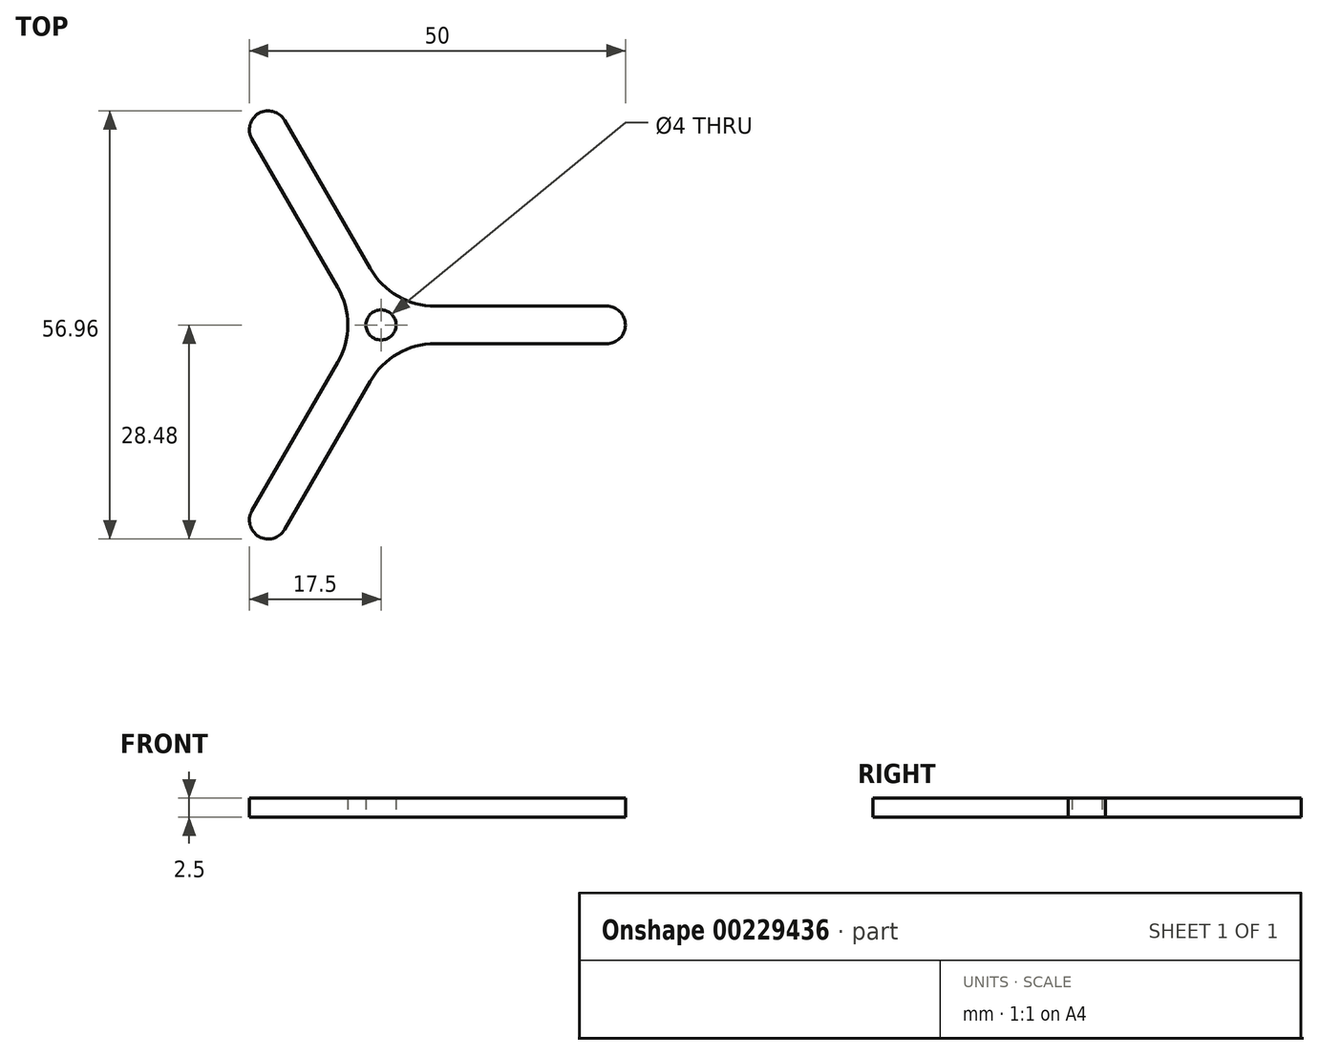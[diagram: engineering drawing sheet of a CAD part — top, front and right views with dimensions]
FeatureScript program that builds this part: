
annotation { "Feature Type Name" : "Feature", "Feature Type Description" : "" }
export const myFeature = defineFeature(function(context is Context, id is Id, definition is map)
    precondition{}
    {
        {
            var Q0;
            Q0=qCreatedBy(makeId("Top.planeOp"),FACE);
            var sketch = newSketch(context, id + "F0", { "sketchPlane" : qUnion([Q0])});
            skCircle(sketch, "E0", {"center": v(30, 0) * mm, "radius": 2.5 * mm});
            skCircle(sketch, "E1", {"center": v(0, 0) * mm, "radius": 2.5 * mm});
            skLineSegment(sketch, "E2", {"start": v(30, 0) * mm, "end": v(0, 0) * mm});
            skLineSegment(sketch, "E3", {"start": v(0, -2.5) * mm, "end": v(30, -2.5) * mm});
            skLineSegment(sketch, "E4.MirrorCS", {"start": v(0, 2.5) * mm, "end": v(30, 2.5) * mm});
            skLineSegment(sketch, "E5.1.1", {"start": v(2.17, 1.25) * mm, "end": v(-12.83, 27.23) * mm});
            skLineSegment(sketch, "E5.1.2", {"start": v(-2.17, -1.25) * mm, "end": v(-17.17, 24.73) * mm});
            skCircle(sketch, "E5.1.3", {"center": v(-15, 25.98) * mm, "radius": 2.5 * mm});
            skLineSegment(sketch, "E5.1.4", {"start": v(-15, 25.98) * mm, "end": v(0, 0) * mm});
            skLineSegment(sketch, "E5.2.1", {"start": v(-2.17, 1.25) * mm, "end": v(-17.17, -24.73) * mm});
            skLineSegment(sketch, "E5.2.2", {"start": v(2.17, -1.25) * mm, "end": v(-12.83, -27.23) * mm});
            skCircle(sketch, "E5.2.3", {"center": v(-15, -25.98) * mm, "radius": 2.5 * mm});
            skLineSegment(sketch, "E5.2.4", {"start": v(-15, -25.98) * mm, "end": v(0, 0) * mm});
            skSolve(sketch);
        }
        {
            var Q0;
            {var subQ0=sQuery(id+"F0.wireOp",EDGE,"E1");var subQ1=makeQuery(id+"F0.imprint","INTERSECT",VERTEX,{"derivedFrom":[sQuery(id+"F0.wireOp",EDGE,"E3"),subQ0]});Q0=makeQuery(id+"F0.imprint","IMPRINT",FACE,{"disambiguationData":[TD([[makeQuery(id+"F0.imprint","IMPRINT",EDGE,{"disambiguationData":[TD([[subQ1,1.0]])],"derivedFrom":subQ0}),1.0]])]});}
            var Q1;
            {var subQ0=sQuery(id+"F0.wireOp",EDGE,"E1");var subQ4=makeQuery(id+"F0.imprint","INTERSECT",VERTEX,{"derivedFrom":[subQ0,sQuery(id+"F0.wireOp",EDGE,"E5.2.1")]});Q1=makeQuery(id+"F0.imprint","IMPRINT",FACE,{"disambiguationData":[TD([[makeQuery(id+"F0.imprint","IMPRINT",EDGE,{"disambiguationData":[TD([[subQ4,1.0]])],"derivedFrom":subQ0}),1.0]])]});}
            var Q2;
            {var subQ0=sQuery(id+"F0.wireOp",EDGE,"E0");var subQ1=makeQuery(id+"F0.imprint","INTERSECT",VERTEX,{"derivedFrom":[subQ0,sQuery(id+"F0.wireOp",EDGE,"E4.MirrorCS")]});Q2=makeQuery(id+"F0.imprint","IMPRINT",FACE,{"disambiguationData":[TD([[makeQuery(id+"F0.imprint","IMPRINT",EDGE,{"disambiguationData":[TD([[subQ1,-1.0]])],"derivedFrom":subQ0}),1.0]])]});}
            var Q3;
            {var subQ0=sQuery(id+"F0.wireOp",EDGE,"E5.1.3");var subQ1=makeQuery(id+"F0.imprint","INTERSECT",VERTEX,{"derivedFrom":[sQuery(id+"F0.wireOp",EDGE,"E5.1.2"),subQ0]});Q3=makeQuery(id+"F0.imprint","IMPRINT",FACE,{"disambiguationData":[TD([[makeQuery(id+"F0.imprint","IMPRINT",EDGE,{"disambiguationData":[TD([[subQ1,-1.0]])],"derivedFrom":subQ0}),1.0]])]});}
            var Q4;
            {var subQ0=sQuery(id+"F0.wireOp",EDGE,"E5.2.3");var subQ1=makeQuery(id+"F0.imprint","INTERSECT",VERTEX,{"derivedFrom":[sQuery(id+"F0.wireOp",EDGE,"E5.2.2"),subQ0]});Q4=makeQuery(id+"F0.imprint","IMPRINT",FACE,{"disambiguationData":[TD([[makeQuery(id+"F0.imprint","IMPRINT",EDGE,{"disambiguationData":[TD([[subQ1,-1.0]])],"derivedFrom":subQ0}),1.0]])]});}
            var Q5;
            {var subQ3=sQuery(id+"F0.wireOp",EDGE,"E4.MirrorCS");var subQ5=sQuery(id+"F0.wireOp",EDGE,"E0");var subQ6=makeQuery(id+"F0.imprint","INTERSECT",VERTEX,{"derivedFrom":[subQ5,subQ3]});Q5=makeQuery(id+"F0.imprint","IMPRINT",FACE,{"disambiguationData":[TD([[makeQuery(id+"F0.imprint","IMPRINT",EDGE,{"disambiguationData":[TD([[subQ6,-1.0]])],"derivedFrom":subQ5}),-1.0]])]});}
            var Q6;
            {var subQ5=sQuery(id+"F0.wireOp",EDGE,"E3");var subQ6=sQuery(id+"F0.wireOp",EDGE,"E0");var subQ7=makeQuery(id+"F0.imprint","INTERSECT",VERTEX,{"derivedFrom":[subQ6,subQ5]});Q6=makeQuery(id+"F0.imprint","IMPRINT",FACE,{"disambiguationData":[TD([[makeQuery(id+"F0.imprint","IMPRINT",EDGE,{"disambiguationData":[TD([[subQ7,1.0]])],"derivedFrom":subQ6}),-1.0]])]});}
            var Q7;
            {var subQ5=sQuery(id+"F0.wireOp",EDGE,"E3");var subQ7=sQuery(id+"F0.wireOp",EDGE,"E1");var subQ8=makeQuery(id+"F0.imprint","INTERSECT",VERTEX,{"derivedFrom":[subQ5,subQ7]});Q7=makeQuery(id+"F0.imprint","IMPRINT",FACE,{"disambiguationData":[TD([[makeQuery(id+"F0.imprint","IMPRINT",EDGE,{"disambiguationData":[TD([[subQ8,-1.0]])],"derivedFrom":subQ5}),-1.0]])]});}
            var Q8;
            {var subQ3=sQuery(id+"F0.wireOp",EDGE,"E1");var subQ7=sQuery(id+"F0.wireOp",EDGE,"E4.MirrorCS");var subQ8=makeQuery(id+"F0.imprint","INTERSECT",VERTEX,{"derivedFrom":[subQ7,subQ3]});Q8=makeQuery(id+"F0.imprint","IMPRINT",FACE,{"disambiguationData":[TD([[makeQuery(id+"F0.imprint","IMPRINT",EDGE,{"disambiguationData":[TD([[subQ8,-1.0]])],"derivedFrom":subQ7}),1.0]])]});}
            var Q9;
            {var subQ5=sQuery(id+"F0.wireOp",EDGE,"E5.1.2");var subQ7=sQuery(id+"F0.wireOp",EDGE,"E1");var subQ8=makeQuery(id+"F0.imprint","INTERSECT",VERTEX,{"derivedFrom":[subQ5,subQ7]});Q9=makeQuery(id+"F0.imprint","IMPRINT",FACE,{"disambiguationData":[TD([[makeQuery(id+"F0.imprint","IMPRINT",EDGE,{"disambiguationData":[TD([[subQ8,-1.0]])],"derivedFrom":subQ5}),1.0]])]});}
            var Q10;
            {var subQ5=sQuery(id+"F0.wireOp",EDGE,"E5.1.3");var subQ6=sQuery(id+"F0.wireOp",EDGE,"E5.1.2");var subQ7=makeQuery(id+"F0.imprint","INTERSECT",VERTEX,{"derivedFrom":[subQ6,subQ5]});Q10=makeQuery(id+"F0.imprint","IMPRINT",FACE,{"disambiguationData":[TD([[makeQuery(id+"F0.imprint","IMPRINT",EDGE,{"disambiguationData":[TD([[subQ7,1.0]])],"derivedFrom":subQ6}),-1.0]])]});}
            var Q11;
            {var subQ3=sQuery(id+"F0.wireOp",EDGE,"E1");var subQ6=makeQuery(id+"F0.imprint","INTERSECT",VERTEX,{"derivedFrom":[sQuery(id+"F0.wireOp",EDGE,"E5.1.1"),subQ3]});Q11=makeQuery(id+"F0.imprint","IMPRINT",FACE,{"disambiguationData":[TD([[makeQuery(id+"F0.imprint","IMPRINT",EDGE,{"disambiguationData":[TD([[subQ6,1.0]])],"derivedFrom":subQ3}),1.0]])]});}
            var Q12;
            {var subQ0=sQuery(id+"F0.wireOp",EDGE,"E1");var subQ1=sQuery(id+"F0.wireOp",EDGE,"E3");var subQ2=makeQuery(id+"F0.imprint","INTERSECT",VERTEX,{"derivedFrom":[subQ1,subQ0]});Q12=makeQuery(id+"F0.imprint","IMPRINT",FACE,{"disambiguationData":[TD([[makeQuery(id+"F0.imprint","IMPRINT",EDGE,{"disambiguationData":[TD([[subQ2,-1.0]])],"derivedFrom":subQ1}),1.0]])]});}
            var Q13;
            {var subQ0=sQuery(id+"F0.wireOp",EDGE,"E1");var subQ1=sQuery(id+"F0.wireOp",EDGE,"E4.MirrorCS");var subQ2=makeQuery(id+"F0.imprint","INTERSECT",VERTEX,{"derivedFrom":[subQ1,subQ0]});Q13=makeQuery(id+"F0.imprint","IMPRINT",FACE,{"disambiguationData":[TD([[makeQuery(id+"F0.imprint","IMPRINT",EDGE,{"disambiguationData":[TD([[subQ2,-1.0]])],"derivedFrom":subQ1}),-1.0]])]});}
            var Q14;
            {var subQ0=sQuery(id+"F0.wireOp",EDGE,"E1");var subQ1=sQuery(id+"F0.wireOp",EDGE,"E5.1.2");var subQ2=makeQuery(id+"F0.imprint","INTERSECT",VERTEX,{"derivedFrom":[subQ1,subQ0]});Q14=makeQuery(id+"F0.imprint","IMPRINT",FACE,{"disambiguationData":[TD([[makeQuery(id+"F0.imprint","IMPRINT",EDGE,{"disambiguationData":[TD([[subQ2,-1.0]])],"derivedFrom":subQ1}),-1.0]])]});}
            extrude(context, id + "F1", {"entities" : qUnion([Q0, Q1, Q2, Q3, Q4, Q5, Q6, Q7, Q8, Q9, Q10, Q11, Q12, Q13, Q14]), "depth" : 2.5 * mm});
        }
        {
            var Q0;
            Q0=qCreatedBy(makeId("Top.planeOp"),FACE);
            var sketch = newSketch(context, id + "F2", { "sketchPlane" : qUnion([Q0])});
            skPoint(sketch, "E6", {"position": v(0, 0) * mm});
            skSolve(sketch);
        }
        {
            var Q0;
            Q0=sQuery(id+"F2.wireOp",VERTEX,"E6");
            var Q1;
            Q1=makeQuery(id+"F1.opExtrude","SWEPT_BODY",BODY,{"disambiguationData":[OSD([sQuery(id+"F0.wireOp",EDGE,"E0"),sQuery(id+"F0.wireOp",EDGE,"E3"),sQuery(id+"F0.wireOp",EDGE,"E4.MirrorCS"),sQuery(id+"F0.wireOp",EDGE,"E5.1.1"),sQuery(id+"F0.wireOp",EDGE,"E5.1.2"),sQuery(id+"F0.wireOp",EDGE,"E5.1.3"),sQuery(id+"F0.wireOp",EDGE,"E5.2.1"),sQuery(id+"F0.wireOp",EDGE,"E5.2.2"),sQuery(id+"F0.wireOp",EDGE,"E5.2.3")])]});
            hole(context, id + "F3", {"style" : HoleStyle.SIMPLE, "endStyle" : HoleEndStyle.THROUGH, "oppositeDirection" : true, "holeDiameter" : 4 * mm, "locations" : qUnion([Q0]), "scope" : qUnion([Q1]), "isTappedThrough" : true});
        }
        {
            var Q0;
            Q0=makeQuery(id+"F1.opExtrude","SWEPT_EDGE",EDGE,{"disambiguationData":[OSD([sQuery(id+"F0.wireOp",EDGE,"E3"),sQuery(id+"F0.wireOp",EDGE,"E5.2.2")])]});
            var Q1;
            Q1=makeQuery(id+"F1.opExtrude","SWEPT_EDGE",EDGE,{"disambiguationData":[OSD([sQuery(id+"F0.wireOp",EDGE,"E5.1.2"),sQuery(id+"F0.wireOp",EDGE,"E5.2.1")])]});
            var Q2;
            Q2=makeQuery(id+"F1.opExtrude","SWEPT_EDGE",EDGE,{"disambiguationData":[OSD([sQuery(id+"F0.wireOp",EDGE,"E4.MirrorCS"),sQuery(id+"F0.wireOp",EDGE,"E5.1.1")])]});
            fillet(context, id + "F4", {"entities" : qUnion([Q0, Q1, Q2]), "radius" : 10 * mm, "tangentPropagation" : true, "allowEdgeOverflow" : false});
        }
    });
